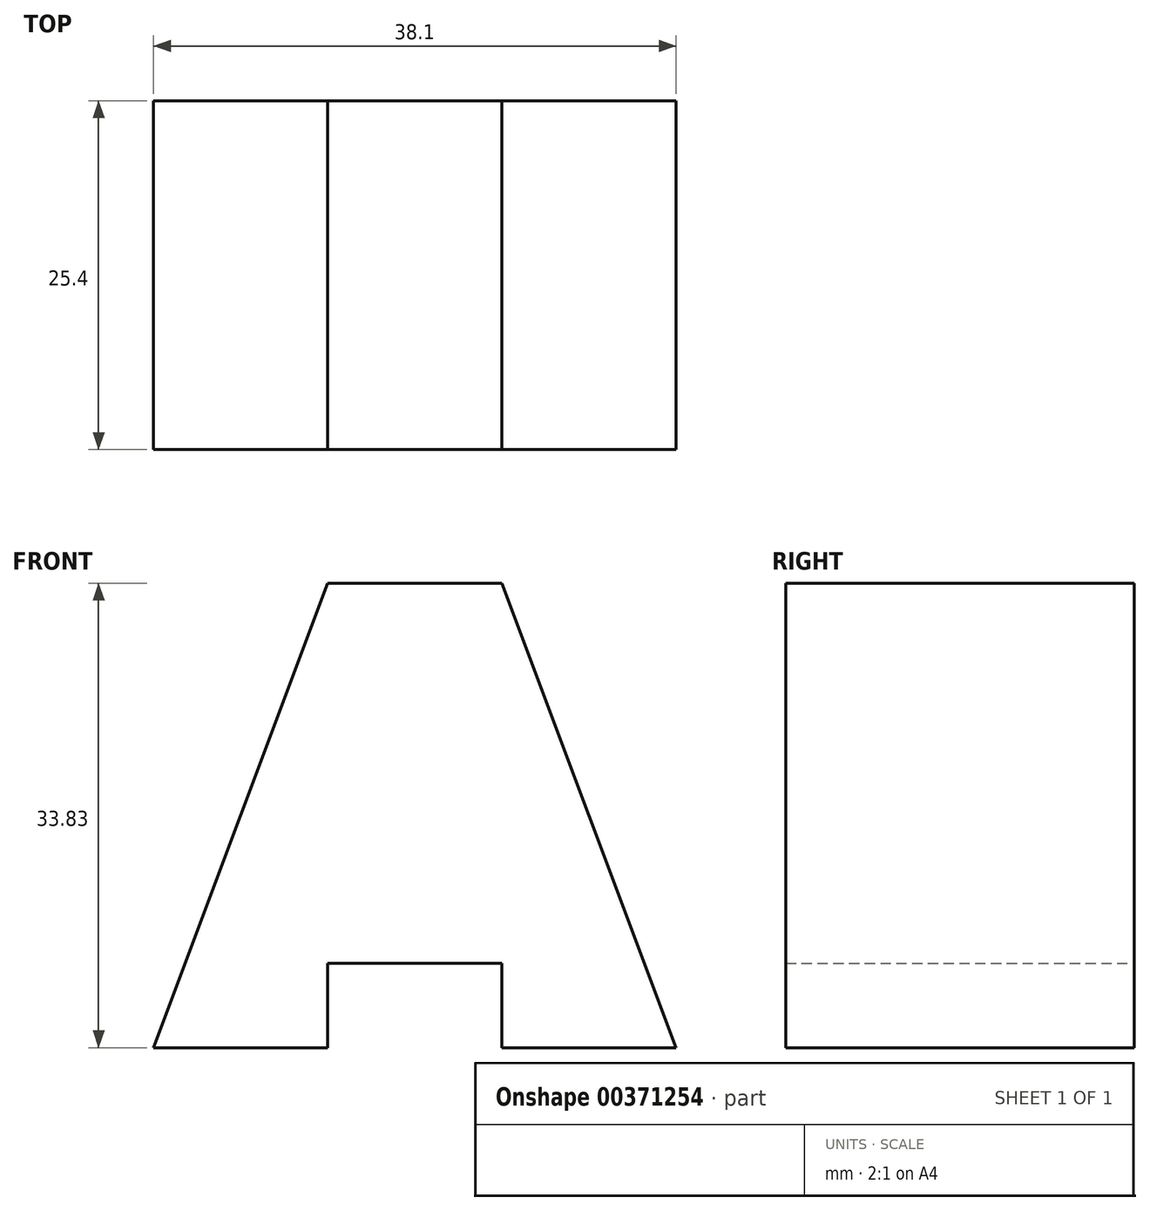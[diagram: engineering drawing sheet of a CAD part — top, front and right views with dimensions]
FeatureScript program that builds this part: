
annotation { "Feature Type Name" : "Feature", "Feature Type Description" : "" }
export const myFeature = defineFeature(function(context is Context, id is Id, definition is map)
    precondition{}
    {
        {
            var Q0;
            Q0=qCreatedBy(makeId("Front.planeOp"),FACE);
            var sketch = newSketch(context, id + "F0", { "sketchPlane" : qUnion([Q0])});
            skLineSegment(sketch, "E0", {"start": v(0, 0) * mm, "end": v(12.7, 0) * mm});
            skLineSegment(sketch, "E1", {"start": v(12.7, 0) * mm, "end": v(12.7, 6.14) * mm});
            skLineSegment(sketch, "E2", {"start": v(12.7, 6.14) * mm, "end": v(25.4, 6.14) * mm});
            skLineSegment(sketch, "E3", {"start": v(25.4, 6.14) * mm, "end": v(25.4, 0) * mm});
            skLineSegment(sketch, "E4", {"start": v(25.4, 0) * mm, "end": v(38.1, 0) * mm});
            skLineSegment(sketch, "E5", {"start": v(38.1, 0) * mm, "end": v(25.4, 33.83) * mm});
            skLineSegment(sketch, "E6", {"start": v(25.4, 33.83) * mm, "end": v(12.7, 33.83) * mm});
            skLineSegment(sketch, "E7", {"start": v(12.7, 33.83) * mm, "end": v(0, 0) * mm});
            skSolve(sketch);
        }
        {
            var Q0;
            Q0=makeQuery(id+"F0.imprint","IMPRINT",FACE,{"disambiguationData":[TD([[makeQuery(id+"F0.imprint","IMPRINT",EDGE,{"derivedFrom":sQuery(id+"F0.wireOp",EDGE,"E0")}),1.0]])]});
            extrude(context, id + "F1", {"entities" : qUnion([Q0]), "depth" : 25.4 * mm});
        }
    });
